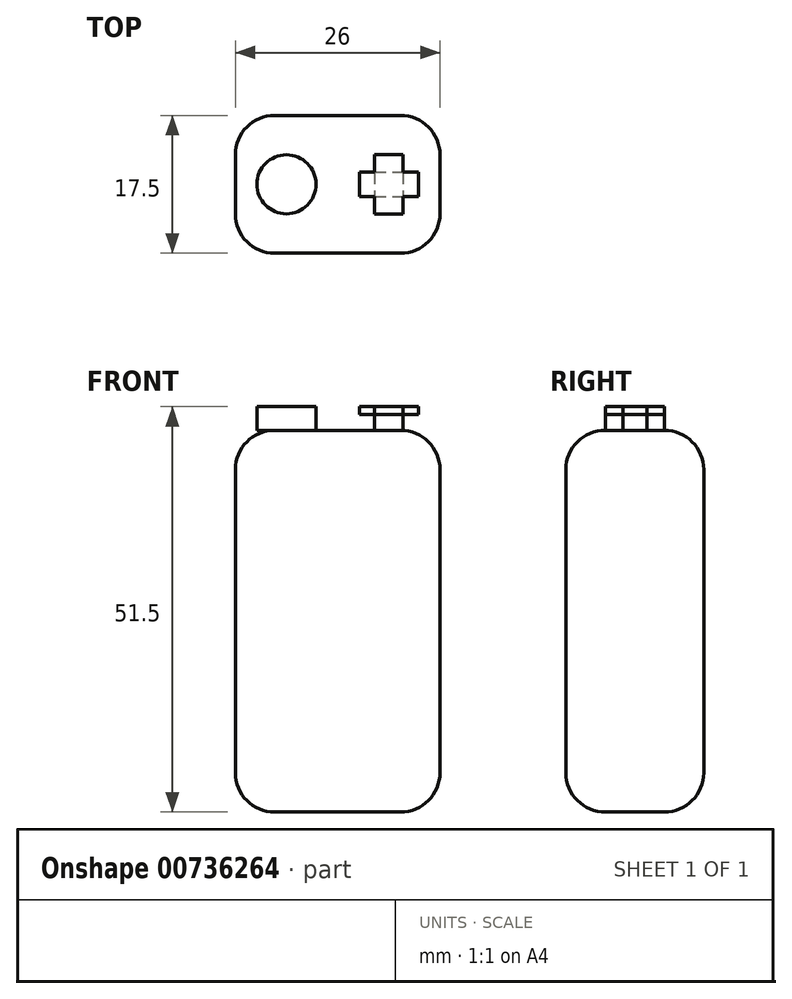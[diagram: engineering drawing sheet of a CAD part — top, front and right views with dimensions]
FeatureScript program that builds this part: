
annotation { "Feature Type Name" : "Feature", "Feature Type Description" : "" }
export const myFeature = defineFeature(function(context is Context, id is Id, definition is map)
    precondition{}
    {
        {
            var Q0;
            Q0=qCreatedBy(makeId("Front.planeOp"),FACE);
            var sketch = newSketch(context, id + "F0", { "sketchPlane" : qUnion([Q0])});
            skLineSegment(sketch, "E0.bottom", {"start": v(-80.01, 30.17) * mm, "end": v(-54.01, 30.17) * mm});
            skLineSegment(sketch, "E0.top", {"start": v(-80.01, -18.33) * mm, "end": v(-54.01, -18.33) * mm});
            skLineSegment(sketch, "E0.left", {"start": v(-80.01, 30.17) * mm, "end": v(-80.01, -18.33) * mm});
            skLineSegment(sketch, "E0.right", {"start": v(-54.01, 30.17) * mm, "end": v(-54.01, -18.33) * mm});
            skSolve(sketch);
        }
        {
            var Q0;
            Q0=makeQuery(id+"F0.imprint","IMPRINT",FACE,{"disambiguationData":[TD([[makeQuery(id+"F0.imprint","IMPRINT",EDGE,{"derivedFrom":sQuery(id+"F0.wireOp",EDGE,"E0.bottom")}),-1.0]])]});
            extrude(context, id + "F1", {"entities" : qUnion([Q0]), "depth" : 17.5 * mm, "offsetDistance" : 25 * mm});
        }
        {
            var Q0;
            Q0=makeQuery(id+"F1.opExtrude","SWEPT_FACE",FACE,{"disambiguationData":[OSD([sQuery(id+"F0.wireOp",EDGE,"E0.bottom")])]});
            var sketch = newSketch(context, id + "F2", { "sketchPlane" : qUnion([Q0])});
            skCircle(sketch, "E1", {"center": v(-73.51, -8.75) * mm, "radius": 3.75 * mm});
            skLineSegment(sketch, "E2.bottom", {"start": v(-62.34, -5) * mm, "end": v(-58.68, -5) * mm});
            skLineSegment(sketch, "E2.top", {"start": v(-62.34, -12.5) * mm, "end": v(-58.68, -12.5) * mm});
            skLineSegment(sketch, "E2.left", {"start": v(-64.26, -7.22) * mm, "end": v(-64.26, -10.28) * mm});
            skLineSegment(sketch, "E2.right", {"start": v(-56.76, -7.22) * mm, "end": v(-56.76, -10.28) * mm});
            skLineSegment(sketch, "E3", {"start": v(-64.26, -7.22) * mm, "end": v(-56.76, -7.22) * mm});
            skLineSegment(sketch, "E4", {"start": v(-64.26, -10.28) * mm, "end": v(-56.76, -10.28) * mm});
            skLineSegment(sketch, "E5", {"start": v(-58.68, -5) * mm, "end": v(-58.68, -12.5) * mm});
            skLineSegment(sketch, "E6", {"start": v(-62.34, -5) * mm, "end": v(-62.34, -12.5) * mm});
            skLineSegment(sketch, "E7", {"start": v(-54.01, -8.75) * mm, "end": v(-80.01, -8.75) * mm, "construction": true});
            skPoint(sketch, "E8.orphan", {"position": v(-56.76, -12.5) * mm});
            skLineSegment(sketch, "E9", {"start": v(-62.34, -5) * mm, "end": v(-58.68, -12.5) * mm, "construction": true});
            skLineSegment(sketch, "E10", {"start": v(-62.34, -12.5) * mm, "end": v(-58.68, -5) * mm, "construction": true});
            skLineSegment(sketch, "E11", {"start": v(-56.76, -7.22) * mm, "end": v(-64.26, -10.28) * mm, "construction": true});
            skLineSegment(sketch, "E12", {"start": v(-64.26, -7.22) * mm, "end": v(-56.76, -10.28) * mm, "construction": true});
            skPoint(sketch, "E13", {"position": v(-60.51, -8.75) * mm});
            skLineSegment(sketch, "E14", {"start": v(-80.01, -8.75) * mm, "end": v(-77.26, -8.75) * mm, "construction": true});
            skLineSegment(sketch, "E15", {"start": v(-56.76, -8.75) * mm, "end": v(-54.01, -8.75) * mm, "construction": true});
            skSolve(sketch);
        }
        {
            var Q0;
            Q0=makeQuery(id+"F2.imprint","IMPRINT",FACE,{"disambiguationData":[TD([[makeQuery(id+"F2.imprint","IMPRINT",EDGE,{"derivedFrom":sQuery(id+"F2.wireOp",EDGE,"E1")}),1.0]])]});
            var Q1;
            {var subQ0=sQuery(id+"F2.wireOp",EDGE,"E6");var subQ1=sQuery(id+"F2.wireOp",EDGE,"E3");var subQ2=makeQuery(id+"F2.imprint","INTERSECT",VERTEX,{"derivedFrom":[subQ1,subQ0]});Q1=makeQuery(id+"F2.imprint","IMPRINT",FACE,{"disambiguationData":[TD([[makeQuery(id+"F2.imprint","IMPRINT",EDGE,{"disambiguationData":[TD([[subQ2,-1.0]])],"derivedFrom":subQ1}),-1.0]])]});}
            extrude(context, id + "F3", {"entities" : qUnion([Q0, Q1]), "depth" : 3 * mm, "offsetDistance" : 25 * mm});
        }
        {
            var Q0;
            Q0=makeQuery(id+"F3.opExtrude","CAP_FACE",FACE,{"disambiguationData":[OSD([sQuery(id+"F2.wireOp",EDGE,"E3"),sQuery(id+"F2.wireOp",EDGE,"E4"),sQuery(id+"F2.wireOp",EDGE,"E5"),sQuery(id+"F2.wireOp",EDGE,"E6")])],"isStart":false});
            var sketch = newSketch(context, id + "F4", { "sketchPlane" : qUnion([Q0])});
            skLineSegment(sketch, "E16.0.0", {"start": v(-58.68, -12.5) * mm, "end": v(-58.68, -10.28) * mm});
            skLineSegment(sketch, "E16.0.1", {"start": v(-58.68, -10.28) * mm, "end": v(-62.34, -10.28) * mm});
            skLineSegment(sketch, "E16.0.2", {"start": v(-62.34, -10.28) * mm, "end": v(-62.34, -12.5) * mm});
            skLineSegment(sketch, "E16.0.3", {"start": v(-62.34, -12.5) * mm, "end": v(-58.68, -12.5) * mm});
            skLineSegment(sketch, "E16.1.0", {"start": v(-62.34, -5) * mm, "end": v(-62.34, -7.22) * mm});
            skLineSegment(sketch, "E16.1.1", {"start": v(-62.34, -7.22) * mm, "end": v(-58.68, -7.22) * mm});
            skLineSegment(sketch, "E16.1.2", {"start": v(-58.68, -7.22) * mm, "end": v(-58.68, -5) * mm});
            skLineSegment(sketch, "E16.1.3", {"start": v(-58.68, -5) * mm, "end": v(-62.34, -5) * mm});
            skLineSegment(sketch, "E16.2.0", {"start": v(-58.68, -7.22) * mm, "end": v(-58.68, -10.28) * mm});
            skLineSegment(sketch, "E16.2.1", {"start": v(-58.68, -10.28) * mm, "end": v(-56.76, -10.28) * mm});
            skLineSegment(sketch, "E16.2.2", {"start": v(-56.76, -10.28) * mm, "end": v(-56.76, -7.22) * mm});
            skLineSegment(sketch, "E16.2.3", {"start": v(-56.76, -7.22) * mm, "end": v(-58.68, -7.22) * mm});
            skLineSegment(sketch, "E16.3.0", {"start": v(-62.34, -10.28) * mm, "end": v(-62.34, -7.22) * mm});
            skLineSegment(sketch, "E16.3.1", {"start": v(-62.34, -7.22) * mm, "end": v(-64.26, -7.22) * mm});
            skLineSegment(sketch, "E16.3.2", {"start": v(-64.26, -7.22) * mm, "end": v(-64.26, -10.28) * mm});
            skLineSegment(sketch, "E16.3.3", {"start": v(-64.26, -10.28) * mm, "end": v(-62.34, -10.28) * mm});
            skSolve(sketch);
        }
        {
            var Q0;
            Q0=makeQuery(id+"F4.imprint","IMPRINT",FACE,{"disambiguationData":[TD([[makeQuery(id+"F4.imprint","IMPRINT",EDGE,{"derivedFrom":sQuery(id+"F4.wireOp",EDGE,"E16.1.0")}),1.0]])]});
            var Q1;
            Q1=makeQuery(id+"F4.imprint","IMPRINT",FACE,{"disambiguationData":[TD([[makeQuery(id+"F4.imprint","IMPRINT",EDGE,{"derivedFrom":sQuery(id+"F4.wireOp",EDGE,"E16.3.0")}),-1.0]])]});
            var Q2;
            Q2=makeQuery(id+"F4.imprint","IMPRINT",FACE,{"disambiguationData":[TD([[makeQuery(id+"F4.imprint","IMPRINT",EDGE,{"derivedFrom":sQuery(id+"F4.wireOp",EDGE,"E16.0.0")}),1.0]])]});
            var Q3;
            Q3=makeQuery(id+"F4.imprint","IMPRINT",FACE,{"disambiguationData":[TD([[makeQuery(id+"F4.imprint","IMPRINT",EDGE,{"derivedFrom":sQuery(id+"F4.wireOp",EDGE,"E16.2.0")}),1.0]])]});
            extrude(context, id + "F5", {"entities" : qUnion([Q0, Q1, Q2, Q3]), "operationType" : NewBodyOperationType.ADD, "oppositeDirection" : true, "depth" : 1 * mm, "offsetDistance" : 25 * mm});
        }
        {
            var Q0;
            Q0=makeQuery(id+"F1.opExtrude","SWEPT_FACE",FACE,{"disambiguationData":[OSD([sQuery(id+"F0.wireOp",EDGE,"E0.right")])]});
            var Q1;
            Q1=makeQuery(id+"F1.opExtrude","SWEPT_FACE",FACE,{"disambiguationData":[OSD([sQuery(id+"F0.wireOp",EDGE,"E0.bottom")])]});
            var Q2;
            Q2=makeQuery(id+"F1.opExtrude","CAP_FACE",FACE,{"disambiguationData":[OSD([sQuery(id+"F0.wireOp",EDGE,"E0.bottom"),sQuery(id+"F0.wireOp",EDGE,"E0.top"),sQuery(id+"F0.wireOp",EDGE,"E0.left"),sQuery(id+"F0.wireOp",EDGE,"E0.right")])],"isStart":true});
            var Q3;
            Q3=makeQuery(id+"F1.opExtrude","CAP_FACE",FACE,{"disambiguationData":[OSD([sQuery(id+"F0.wireOp",EDGE,"E0.bottom"),sQuery(id+"F0.wireOp",EDGE,"E0.top"),sQuery(id+"F0.wireOp",EDGE,"E0.left"),sQuery(id+"F0.wireOp",EDGE,"E0.right")])],"isStart":false});
            var Q4;
            Q4=makeQuery(id+"F1.opExtrude","SWEPT_FACE",FACE,{"disambiguationData":[OSD([sQuery(id+"F0.wireOp",EDGE,"E0.left")])]});
            fillet(context, id + "F6", {"entities" : qUnion([Q0, Q1, Q2, Q3, Q4]), "radius" : 5 * mm, "tangentPropagation" : true, "allowEdgeOverflow" : false});
        }
    });
